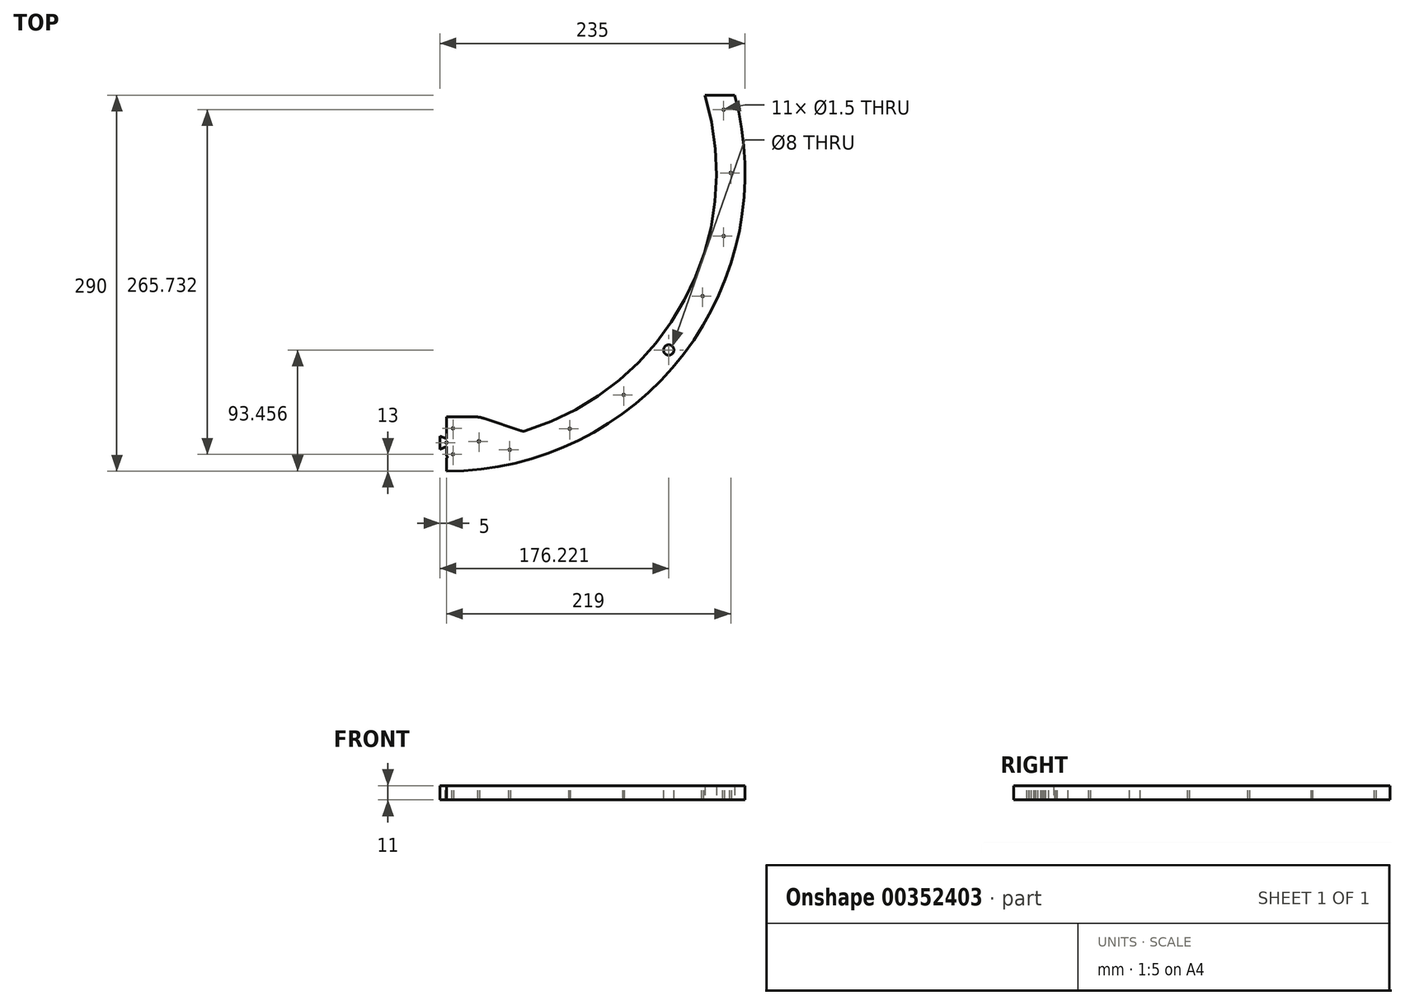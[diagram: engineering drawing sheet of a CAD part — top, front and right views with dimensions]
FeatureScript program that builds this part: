
annotation { "Feature Type Name" : "Feature", "Feature Type Description" : "" }
export const myFeature = defineFeature(function(context is Context, id is Id, definition is map)
    precondition{}
    {
        {
            var Q0;
            Q0=qCreatedBy(makeId("Top.planeOp"),FACE);
            var sketch = newSketch(context, id + "F0", { "sketchPlane" : qUnion([Q0])});
            skArc(sketch, "E0", {"start": v(-199.16, 60) * mm, "mid": v(-183.03, -98.8) * mm, "end": v(-59.12, -199.42) * mm});
            skArc(sketch, "E1", {"start": v(-222.04, 60) * mm, "mid": v(0, -230) * mm, "end": v(222.04, 60) * mm});
            skLineSegment(sketch, "E2", {"start": v(0, 0) * mm, "end": v(-114.72, 0) * mm, "construction": true});
            skLineSegment(sketch, "E3", {"start": v(0, 0) * mm, "end": v(0, 60) * mm, "construction": true});
            skLineSegment(sketch, "E4", {"start": v(199.16, 60) * mm, "end": v(222.04, 60) * mm});
            skLineSegment(sketch, "E5.MirrorCS", {"start": v(-199.16, 60) * mm, "end": v(-222.04, 60) * mm});
            skLineSegment(sketch, "E6", {"start": v(0, -208) * mm, "end": v(0, -188) * mm, "construction": true});
            skLineSegment(sketch, "E7", {"start": v(0, -188) * mm, "end": v(25, -188) * mm});
            skLineSegment(sketch, "E8", {"start": v(25, -188) * mm, "end": v(59.12, -199.42) * mm});
            skLineSegment(sketch, "E9.MirrorCS", {"start": v(0, -188) * mm, "end": v(-25, -188) * mm});
            skLineSegment(sketch, "E10.MirrorCS", {"start": v(-25, -188) * mm, "end": v(-59.12, -199.42) * mm});
            skArc(sketch, "E11.trimOffspring", {"start": v(59.12, -199.42) * mm, "mid": v(183.03, -98.8) * mm, "end": v(199.16, 60) * mm});
            skPoint(sketch, "E12.orphan", {"position": v(0, 60) * mm});
            skSolve(sketch);
        }
        {
            var Q0;
            Q0=qSketchRegion(id+"F0",true);
            extrude(context, id + "F1", {"entities" : qUnion([Q0]), "depth" : 11 * mm});
        }
        {
            var Q0;
            Q0=makeQuery(id+"F1.opExtrude","SWEPT_EDGE",EDGE,{"disambiguationData":[OSD([sQuery(id+"F0.wireOp",EDGE,"E7"),sQuery(id+"F0.wireOp",EDGE,"E8")])]});
            var Q1;
            Q1=makeQuery(id+"F1.opExtrude","SWEPT_EDGE",EDGE,{"disambiguationData":[OSD([sQuery(id+"F0.wireOp",EDGE,"E9.MirrorCS"),sQuery(id+"F0.wireOp",EDGE,"E10.MirrorCS")])]});
            fillet(context, id + "F2", {"entities" : qUnion([Q0, Q1]), "radius" : 28.52 * mm, "tangentPropagation" : true, "allowEdgeOverflow" : false});
        }
        {
            var Q0;
            Q0=makeQuery(id+"F1.opExtrude","SWEPT_EDGE",EDGE,{"disambiguationData":[OSD([sQuery(id+"F0.wireOp",EDGE,"E8"),sQuery(id+"F0.wireOp",EDGE,"E11.trimOffspring")])]});
            var Q1;
            Q1=makeQuery(id+"F1.opExtrude","SWEPT_EDGE",EDGE,{"disambiguationData":[OSD([sQuery(id+"F0.wireOp",EDGE,"E0"),sQuery(id+"F0.wireOp",EDGE,"E10.MirrorCS")])]});
            fillet(context, id + "F3", {"entities" : qUnion([Q0, Q1]), "radius" : 5 * mm, "tangentPropagation" : true, "allowEdgeOverflow" : false});
        }
        {
            var Q0;
            Q0=qCreatedBy(makeId("Top.planeOp"),FACE);
            var sketch = newSketch(context, id + "F4", { "sketchPlane" : qUnion([Q0])});
            skLineSegment(sketch, "E13", {"start": v(0, 0) * mm, "end": v(174.2, -171.38) * mm, "construction": true});
            skLineSegment(sketch, "E14", {"start": v(0, 0) * mm, "end": v(0, 36.6) * mm, "construction": true});
            skLineSegment(sketch, "E15.MirrorCS", {"start": v(0, 0) * mm, "end": v(-174.2, -171.38) * mm, "construction": true});
            skSolve(sketch);
        }
        {
            var Q0;
            Q0=makeQuery(id+"F1.opExtrude","CAP_FACE",FACE,{"disambiguationData":[OSD([sQuery(id+"F0.wireOp",EDGE,"E0"),sQuery(id+"F0.wireOp",EDGE,"E1"),sQuery(id+"F0.wireOp",EDGE,"E4"),sQuery(id+"F0.wireOp",EDGE,"E5.MirrorCS"),sQuery(id+"F0.wireOp",EDGE,"E7"),sQuery(id+"F0.wireOp",EDGE,"E8"),sQuery(id+"F0.wireOp",EDGE,"E9.MirrorCS"),sQuery(id+"F0.wireOp",EDGE,"E10.MirrorCS"),sQuery(id+"F0.wireOp",EDGE,"E11.trimOffspring")])],"isStart":false});
            var sketch = newSketch(context, id + "F5", { "sketchPlane" : qUnion([Q0])});
            skArc(sketch, "E16.0", {"start": v(-217.44, 26.07) * mm, "mid": v(0, -219) * mm, "end": v(217.44, 26.07) * mm, "construction": true});
            skCircle(sketch, "E17", {"center": v(0, -219) * mm, "radius": 0.75 * mm});
            skCircle(sketch, "E18.1.0", {"center": v(48.73, -213.5) * mm, "radius": 0.75 * mm});
            skCircle(sketch, "E18.2.0", {"center": v(95.02, -197.31) * mm, "radius": 0.75 * mm});
            skCircle(sketch, "E18.3.0", {"center": v(136.54, -171.22) * mm, "radius": 0.75 * mm});
            skCircle(sketch, "E18.4.0", {"center": v(171.22, -136.54) * mm, "radius": 0.75 * mm});
            skCircle(sketch, "E18.5.0", {"center": v(197.31, -95.02) * mm, "radius": 0.75 * mm});
            skCircle(sketch, "E18.6.0", {"center": v(213.5, -48.73) * mm, "radius": 0.75 * mm});
            skCircle(sketch, "E18.7.0", {"center": v(219, 0) * mm, "radius": 0.75 * mm});
            skCircle(sketch, "E18.8.0", {"center": v(213.5, 48.73) * mm, "radius": 0.75 * mm});
            skCircle(sketch, "E18.9.0", {"center": v(197.31, 95.02) * mm, "radius": 0.75 * mm});
            skCircle(sketch, "E18.10.0", {"center": v(171.22, 136.54) * mm, "radius": 0.75 * mm});
            skCircle(sketch, "E18.11.0", {"center": v(136.54, 171.22) * mm, "radius": 0.75 * mm});
            skCircle(sketch, "E18.12.0", {"center": v(95.02, 197.31) * mm, "radius": 0.75 * mm});
            skCircle(sketch, "E18.13.0", {"center": v(48.73, 213.5) * mm, "radius": 0.75 * mm});
            skCircle(sketch, "E18.14.0", {"center": v(0, 219) * mm, "radius": 0.75 * mm});
            skCircle(sketch, "E18.15.0", {"center": v(-48.73, 213.5) * mm, "radius": 0.75 * mm});
            skCircle(sketch, "E18.16.0", {"center": v(-95.02, 197.31) * mm, "radius": 0.75 * mm});
            skCircle(sketch, "E18.17.0", {"center": v(-136.54, 171.22) * mm, "radius": 0.75 * mm});
            skCircle(sketch, "E18.18.0", {"center": v(-171.22, 136.54) * mm, "radius": 0.75 * mm});
            skCircle(sketch, "E18.19.0", {"center": v(-197.31, 95.02) * mm, "radius": 0.75 * mm});
            skCircle(sketch, "E18.20.0", {"center": v(-213.5, 48.73) * mm, "radius": 0.75 * mm});
            skCircle(sketch, "E18.21.0", {"center": v(-219, 0) * mm, "radius": 0.75 * mm});
            skCircle(sketch, "E18.22.0", {"center": v(-213.5, -48.73) * mm, "radius": 0.75 * mm});
            skCircle(sketch, "E18.23.0", {"center": v(-197.31, -95.02) * mm, "radius": 0.75 * mm});
            skCircle(sketch, "E18.24.0", {"center": v(-171.22, -136.54) * mm, "radius": 0.75 * mm});
            skCircle(sketch, "E18.25.0", {"center": v(-136.54, -171.22) * mm, "radius": 0.75 * mm});
            skCircle(sketch, "E18.26.0", {"center": v(-95.02, -197.31) * mm, "radius": 0.75 * mm});
            skCircle(sketch, "E18.27.0", {"center": v(-48.73, -213.5) * mm, "radius": 0.75 * mm});
            skCircle(sketch, "E19", {"center": v(-5, -197) * mm, "radius": 0.75 * mm});
            skLineSegment(sketch, "E20", {"start": v(0, 0) * mm, "end": v(0, -93.12) * mm, "construction": true});
            skLineSegment(sketch, "E21", {"start": v(0, -219) * mm, "end": v(0, -197) * mm, "construction": true});
            skLineSegment(sketch, "E22", {"start": v(0, -197) * mm, "end": v(-5, -197) * mm, "construction": true});
            skCircle(sketch, "E23.MirrorC", {"center": v(5, -197) * mm, "radius": 0.75 * mm});
            skLineSegment(sketch, "E24", {"start": v(-5, -197) * mm, "end": v(-5, -217) * mm, "construction": true});
            skPoint(sketch, "E25.endSnap0", {"position": v(-5, -207) * mm});
            skLineSegment(sketch, "E26", {"start": v(-5, -207) * mm, "end": v(-25, -207) * mm, "construction": true});
            skCircle(sketch, "E27", {"center": v(0, -208) * mm, "radius": 0.75 * mm});
            skCircle(sketch, "E28.MirrorC", {"center": v(-5, -217) * mm, "radius": 0.75 * mm});
            skCircle(sketch, "E29", {"center": v(-25, -207) * mm, "radius": 0.75 * mm});
            skCircle(sketch, "E30.MirrorC", {"center": v(5, -217) * mm, "radius": 0.75 * mm});
            skCircle(sketch, "E31.MirrorC", {"center": v(25, -207) * mm, "radius": 0.75 * mm});
            skSolve(sketch);
        }
        {
            var Q0;
            Q0=qSketchRegion(id+"F5",true);
            extrude(context, id + "F6", {"entities" : qUnion([Q0]), "operationType" : NewBodyOperationType.REMOVE, "endBound" : BoundingType.THROUGH_ALL, "oppositeDirection" : true, "depth" : 25 * mm});
        }
        {
            var Q0;
            Q0=makeQuery(id+"F1.opExtrude","CAP_FACE",FACE,{"disambiguationData":[OSD([sQuery(id+"F0.wireOp",EDGE,"E0"),sQuery(id+"F0.wireOp",EDGE,"E1"),sQuery(id+"F0.wireOp",EDGE,"E4"),sQuery(id+"F0.wireOp",EDGE,"E5.MirrorCS"),sQuery(id+"F0.wireOp",EDGE,"E7"),sQuery(id+"F0.wireOp",EDGE,"E8"),sQuery(id+"F0.wireOp",EDGE,"E9.MirrorCS"),sQuery(id+"F0.wireOp",EDGE,"E10.MirrorCS"),sQuery(id+"F0.wireOp",EDGE,"E11.trimOffspring")])],"isStart":false});
            var sketch = newSketch(context, id + "F7", { "sketchPlane" : qUnion([Q0])});
            skCircle(sketch, "E32", {"center": v(-171.22, -136.54) * mm, "radius": 4 * mm});
            skLineSegment(sketch, "E33", {"start": v(0, 0) * mm, "end": v(0, -100.25) * mm, "construction": true});
            skCircle(sketch, "E34.MirrorC", {"center": v(171.22, -136.54) * mm, "radius": 4 * mm});
            skSolve(sketch);
        }
        {
            var Q0;
            Q0=qSketchRegion(id+"F7",true);
            extrude(context, id + "F8", {"entities" : qUnion([Q0]), "operationType" : NewBodyOperationType.REMOVE, "endBound" : BoundingType.THROUGH_ALL, "oppositeDirection" : true, "depth" : 25 * mm});
        }
        {
            var Q0;
            Q0=makeQuery(id+"F1.opExtrude","CAP_FACE",FACE,{"disambiguationData":[OSD([sQuery(id+"F0.wireOp",EDGE,"E0"),sQuery(id+"F0.wireOp",EDGE,"E1"),sQuery(id+"F0.wireOp",EDGE,"E4"),sQuery(id+"F0.wireOp",EDGE,"E5.MirrorCS"),sQuery(id+"F0.wireOp",EDGE,"E7"),sQuery(id+"F0.wireOp",EDGE,"E8"),sQuery(id+"F0.wireOp",EDGE,"E9.MirrorCS"),sQuery(id+"F0.wireOp",EDGE,"E10.MirrorCS"),sQuery(id+"F0.wireOp",EDGE,"E11.trimOffspring")])],"isStart":false});
            var sketch = newSketch(context, id + "F9", { "sketchPlane" : qUnion([Q0])});
            skLineSegment(sketch, "E35", {"start": v(0, -188) * mm, "end": v(0, 106.2) * mm});
            skLineSegment(sketch, "E36", {"start": v(0, 106.2) * mm, "end": v(-257.95, 106.2) * mm});
            skLineSegment(sketch, "E37", {"start": v(-257.95, 106.2) * mm, "end": v(-257.95, -251.47) * mm});
            skLineSegment(sketch, "E38", {"start": v(-257.95, -251.47) * mm, "end": v(0, -251.47) * mm});
            skPoint(sketch, "E38.endSnap0", {"position": v(0, -230) * mm});
            skLineSegment(sketch, "E39", {"start": v(0, -188) * mm, "end": v(0, -205) * mm});
            skLineSegment(sketch, "E40", {"start": v(0, -211) * mm, "end": v(0, -251.47) * mm});
            skLineSegment(sketch, "E41", {"start": v(0, -208) * mm, "end": v(0, -205) * mm, "construction": true});
            skLineSegment(sketch, "E42", {"start": v(0, -208) * mm, "end": v(0, -211) * mm, "construction": true});
            skLineSegment(sketch, "E43", {"start": v(0, -205) * mm, "end": v(-5, -202.92) * mm});
            skLineSegment(sketch, "E44", {"start": v(0, -208) * mm, "end": v(7.63, -208) * mm, "construction": true});
            skLineSegment(sketch, "E45.MirrorCS", {"start": v(0, -211) * mm, "end": v(-5, -213.08) * mm});
            skLineSegment(sketch, "E46", {"start": v(-5, -202.92) * mm, "end": v(-5, -213.08) * mm});
            skSolve(sketch);
        }
        {
            var Q0;
            Q0 = qSketchRegion(id + "F9", true);
            extrude(context, id + "F10", {"entities" : qUnion([Q0]), "operationType" : NewBodyOperationType.REMOVE, "endBound" : BoundingType.THROUGH_ALL, "oppositeDirection" : true, "depth" : 25 * mm});
        }
    });
